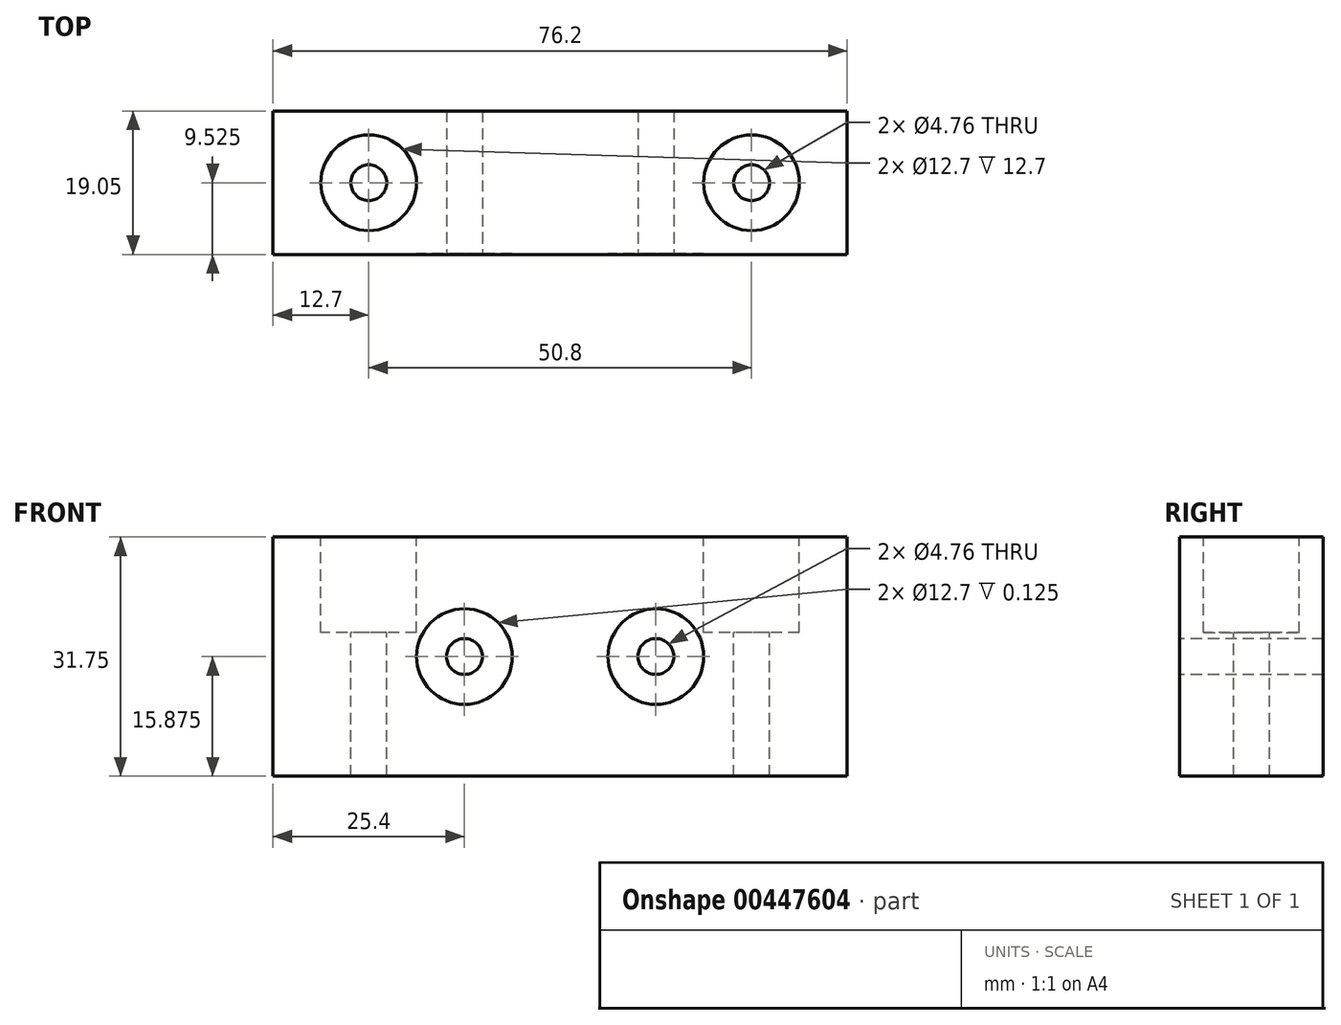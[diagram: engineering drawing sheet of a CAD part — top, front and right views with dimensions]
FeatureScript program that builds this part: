
annotation { "Feature Type Name" : "Feature", "Feature Type Description" : "" }
export const myFeature = defineFeature(function(context is Context, id is Id, definition is map)
    precondition{}
    {
        {
            var Q0;
            Q0=qCreatedBy(makeId("Front.planeOp"),FACE);
            var sketch = newSketch(context, id + "F0", { "sketchPlane" : qUnion([Q0])});
            skLineSegment(sketch, "E0.bottom", {"start": v(0, 0) * mm, "end": v(76.2, 0) * mm});
            skLineSegment(sketch, "E0.top", {"start": v(0, 31.75) * mm, "end": v(76.2, 31.75) * mm});
            skLineSegment(sketch, "E0.left", {"start": v(0, 0) * mm, "end": v(0, 31.75) * mm});
            skLineSegment(sketch, "E0.right", {"start": v(76.2, 0) * mm, "end": v(76.2, 31.75) * mm});
            skSolve(sketch);
        }
        {
            var Q0;
            Q0 = qSketchRegion(id + "F0", true);
            extrude(context, id + "F1", {"entities" : qUnion([Q0]), "depth" : 19.05 * mm, "offsetDistance" : 25.4 * mm});
        }
        {
            var Q0;
            Q0=makeQuery(id+"F1.opExtrude","SWEPT_FACE",FACE,{"disambiguationData":[OSD([sQuery(id+"F0.wireOp",EDGE,"E0.top")])]});
            var sketch = newSketch(context, id + "F2", { "sketchPlane" : qUnion([Q0])});
            skCircle(sketch, "E1", {"center": v(12.7, -9.53) * mm, "radius": 2.38 * mm});
            skCircle(sketch, "E2", {"center": v(63.5, -9.53) * mm, "radius": 2.38 * mm});
            skSolve(sketch);
        }
        {
            var Q0;
            Q0 = qSketchRegion(id + "F2", true);
            extrude(context, id + "F3", {"entities" : qUnion([Q0]), "operationType" : NewBodyOperationType.REMOVE, "endBound" : BoundingType.THROUGH_ALL, "oppositeDirection" : true, "depth" : 25.4 * mm, "offsetDistance" : 25.4 * mm});
        }
        {
            var Q0;
            Q0=makeQuery(id+"F1.opExtrude","SWEPT_FACE",FACE,{"disambiguationData":[OSD([sQuery(id+"F0.wireOp",EDGE,"E0.top")])]});
            var sketch = newSketch(context, id + "F4", { "sketchPlane" : qUnion([Q0])});
            skCircle(sketch, "E3", {"center": v(12.7, -9.53) * mm, "radius": 6.35 * mm});
            skCircle(sketch, "E4", {"center": v(63.5, -9.53) * mm, "radius": 6.35 * mm});
            skSolve(sketch);
        }
        {
            var Q0;
            Q0 = qSketchRegion(id + "F4", true);
            extrude(context, id + "F5", {"entities" : qUnion([Q0]), "operationType" : NewBodyOperationType.REMOVE, "oppositeDirection" : true, "depth" : 12.7 * mm, "offsetDistance" : 25.4 * mm});
        }
        {
            var Q0;
            Q0=makeQuery(id+"F1.opExtrude","CAP_FACE",FACE,{"disambiguationData":[OSD([sQuery(id+"F0.wireOp",EDGE,"E0.bottom"),sQuery(id+"F0.wireOp",EDGE,"E0.top"),sQuery(id+"F0.wireOp",EDGE,"E0.left"),sQuery(id+"F0.wireOp",EDGE,"E0.right")])],"isStart":false});
            var sketch = newSketch(context, id + "F6", { "sketchPlane" : qUnion([Q0])});
            skCircle(sketch, "E5", {"center": v(50.8, 15.88) * mm, "radius": 2.38 * mm});
            skCircle(sketch, "E6", {"center": v(25.4, 15.88) * mm, "radius": 2.38 * mm});
            skSolve(sketch);
        }
        {
            var Q0;
            Q0 = qSketchRegion(id + "F6", true);
            extrude(context, id + "F7", {"entities" : qUnion([Q0]), "operationType" : NewBodyOperationType.REMOVE, "endBound" : BoundingType.THROUGH_ALL, "oppositeDirection" : true, "depth" : 25.4 * mm, "offsetDistance" : 25.4 * mm});
        }
        {
            var Q0;
            Q0=makeQuery(id+"F1.opExtrude","CAP_FACE",FACE,{"disambiguationData":[OSD([sQuery(id+"F0.wireOp",EDGE,"E0.bottom"),sQuery(id+"F0.wireOp",EDGE,"E0.top"),sQuery(id+"F0.wireOp",EDGE,"E0.left"),sQuery(id+"F0.wireOp",EDGE,"E0.right")])],"isStart":false});
            var sketch = newSketch(context, id + "F8", { "sketchPlane" : qUnion([Q0])});
            skCircle(sketch, "E7", {"center": v(25.4, 15.88) * mm, "radius": 6.35 * mm});
            skCircle(sketch, "E8", {"center": v(50.8, 15.88) * mm, "radius": 6.35 * mm});
            skSolve(sketch);
        }
        {
            var Q0;
            Q0 = qSketchRegion(id + "F8", true);
            extrude(context, id + "F9", {"entities" : qUnion([Q0]), "operationType" : NewBodyOperationType.REMOVE, "oppositeDirection" : true, "depth" : ((1.5 - 1.25) / 2) * mm, "offsetDistance" : 25.4 * mm});
        }
    });
